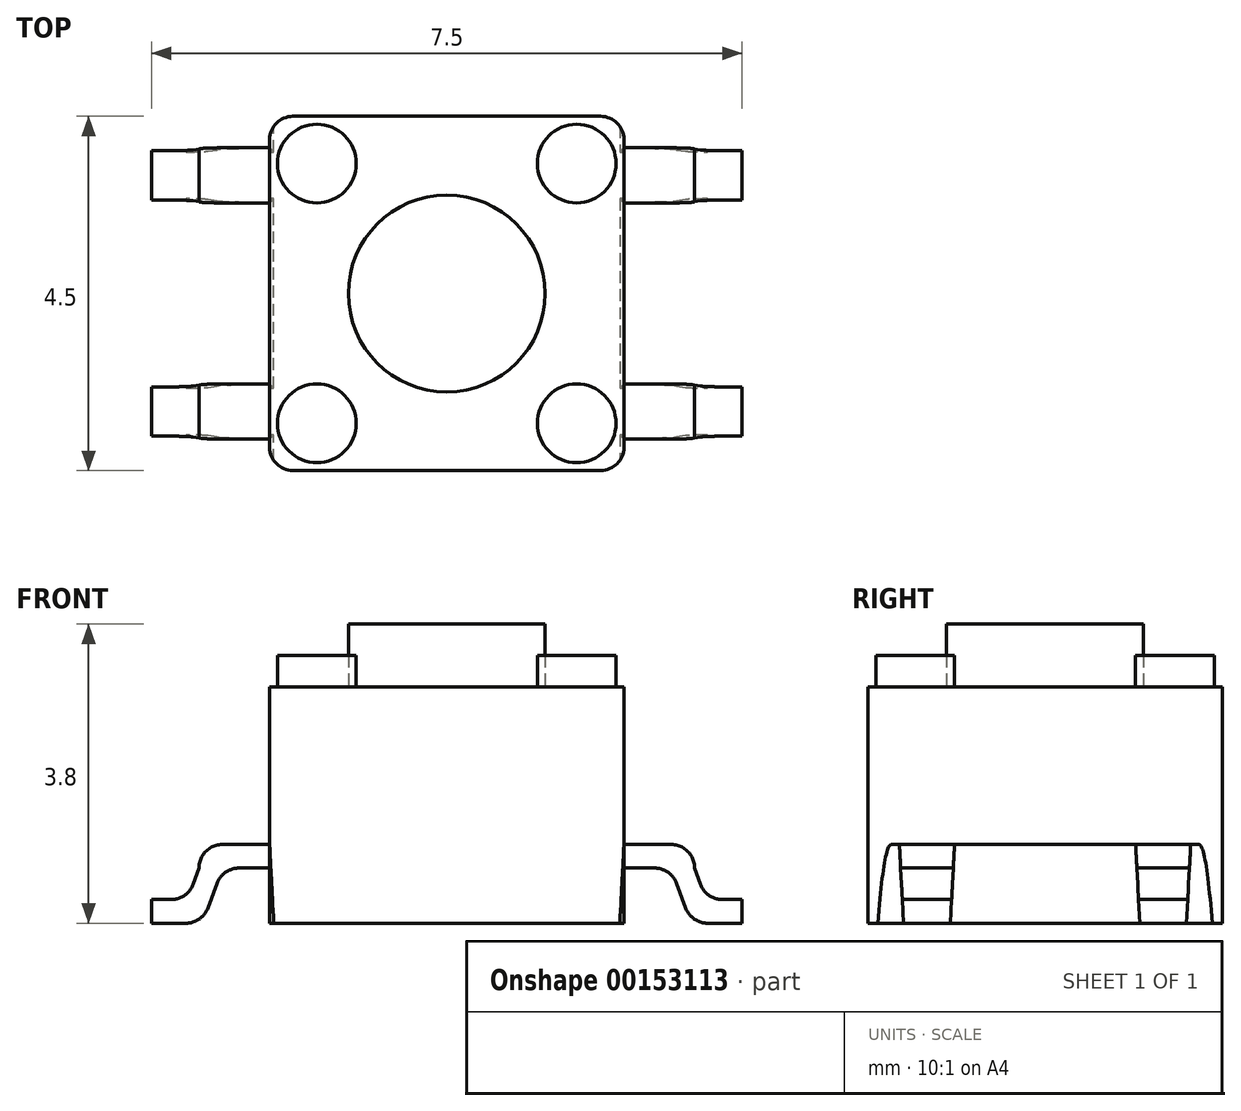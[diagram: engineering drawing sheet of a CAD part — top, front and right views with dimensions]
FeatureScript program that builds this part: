
annotation { "Feature Type Name" : "Feature", "Feature Type Description" : "" }
export const myFeature = defineFeature(function(context is Context, id is Id, definition is map)
    precondition{}
    {
        {
            var Q0;
            Q0=qCreatedBy(makeId("Top.planeOp"),FACE);
            var sketch = newSketch(context, id + "F0", { "sketchPlane" : qUnion([Q0])});
            skLineSegment(sketch, "E0.bottom", {"start": v(-1.96, 2.25) * mm, "end": v(1.96, 2.25) * mm});
            skLineSegment(sketch, "E0.top", {"start": v(-1.96, -2.25) * mm, "end": v(1.96, -2.25) * mm});
            skLineSegment(sketch, "E0.left", {"start": v(-2.25, 1.96) * mm, "end": v(-2.25, -1.96) * mm});
            skLineSegment(sketch, "E0.right", {"start": v(2.25, 1.96) * mm, "end": v(2.25, -1.96) * mm});
            skPoint(sketch, "E1.visualSharp", {"position": v(-2.25, 2.25) * mm});
            skArc(sketch, "E1.filletArc", {"start": v(-1.96, 2.25) * mm, "mid": v(-2.16, 2.16) * mm, "end": v(-2.25, 1.96) * mm});
            skPoint(sketch, "E2.visualSharp", {"position": v(-2.25, -2.25) * mm});
            skArc(sketch, "E2.filletArc", {"start": v(-2.25, -1.96) * mm, "mid": v(-2.16, -2.16) * mm, "end": v(-1.96, -2.25) * mm});
            skPoint(sketch, "E3.visualSharp", {"position": v(2.25, -2.25) * mm});
            skArc(sketch, "E3.filletArc", {"start": v(1.96, -2.25) * mm, "mid": v(2.16, -2.16) * mm, "end": v(2.25, -1.96) * mm});
            skPoint(sketch, "E4.visualSharp", {"position": v(2.25, 2.25) * mm});
            skArc(sketch, "E4.filletArc", {"start": v(2.25, 1.96) * mm, "mid": v(2.16, 2.16) * mm, "end": v(1.96, 2.25) * mm});
            skSolve(sketch);
        }
        {
            var Q0;
            Q0 = qSketchRegion(id + "F0", true);
            extrude(context, id + "F1", {"entities" : qUnion([Q0]), "depth" : 3 * mm});
        }
        {
            var Q0;
            Q0=makeQuery(id+"F1.opExtrude","CAP_FACE",FACE,{"disambiguationData":[OSD([sQuery(id+"F0.wireOp",EDGE,"E0.bottom"),sQuery(id+"F0.wireOp",EDGE,"E0.top"),sQuery(id+"F0.wireOp",EDGE,"E0.left"),sQuery(id+"F0.wireOp",EDGE,"E0.right"),sQuery(id+"F0.wireOp",EDGE,"E1.filletArc"),sQuery(id+"F0.wireOp",EDGE,"E2.filletArc"),sQuery(id+"F0.wireOp",EDGE,"E3.filletArc"),sQuery(id+"F0.wireOp",EDGE,"E4.filletArc")])],"isStart":false});
            var sketch = newSketch(context, id + "F2", { "sketchPlane" : qUnion([Q0])});
            skCircle(sketch, "E5", {"center": v(0, 0) * mm, "radius": 1.25 * mm});
            skSolve(sketch);
        }
        {
            var Q0;
            Q0 = qSketchRegion(id + "F2", true);
            extrude(context, id + "F3", {"entities" : qUnion([Q0]), "depth" : .8 * mm});
        }
        {
            var Q0;
            Q0=makeQuery(id+"F1.opExtrude","CAP_FACE",FACE,{"disambiguationData":[OSD([sQuery(id+"F0.wireOp",EDGE,"E0.bottom"),sQuery(id+"F0.wireOp",EDGE,"E0.top"),sQuery(id+"F0.wireOp",EDGE,"E0.left"),sQuery(id+"F0.wireOp",EDGE,"E0.right"),sQuery(id+"F0.wireOp",EDGE,"E1.filletArc"),sQuery(id+"F0.wireOp",EDGE,"E2.filletArc"),sQuery(id+"F0.wireOp",EDGE,"E3.filletArc"),sQuery(id+"F0.wireOp",EDGE,"E4.filletArc")])],"isStart":false});
            var sketch = newSketch(context, id + "F4", { "sketchPlane" : qUnion([Q0])});
            skCircle(sketch, "E6", {"center": v(-1.65, 1.65) * mm, "radius": 0.5 * mm});
            skCircle(sketch, "E7.MirrorC", {"center": v(1.65, 1.65) * mm, "radius": 0.5 * mm});
            skCircle(sketch, "E8.MirrorC", {"center": v(1.65, -1.65) * mm, "radius": 0.5 * mm});
            skCircle(sketch, "E9.MirrorC", {"center": v(-1.65, -1.65) * mm, "radius": 0.5 * mm});
            skSolve(sketch);
        }
        {
            var Q0;
            Q0 = qSketchRegion(id + "F4", true);
            extrude(context, id + "F5", {"entities" : qUnion([Q0]), "operationType" : NewBodyOperationType.ADD, "depth" : .4 * mm});
        }
        {
            var Q0;
            Q0=makeQuery(id+"F1.opExtrude","SWEPT_FACE",FACE,{"disambiguationData":[OSD([sQuery(id+"F0.wireOp",EDGE,"E0.top")])]});
            var sketch = newSketch(context, id + "F6", { "sketchPlane" : qUnion([Q0])});
            skLineSegment(sketch, "E10", {"start": v(-2.25, 3) * mm, "end": v(-2.25, 0) * mm});
            skLineSegment(sketch, "E11.left", {"start": v(-3.75, 0) * mm, "end": v(-3.75, 0.3) * mm});
            skLineSegment(sketch, "E12.right", {"start": v(-2.25, 1) * mm, "end": v(-2.25, 0.7) * mm});
            skLineSegment(sketch, "E13", {"start": v(-3.22, 0.5) * mm, "end": v(-3.15, 0.7) * mm});
            skLineSegment(sketch, "E14", {"start": v(-3, 0.3) * mm, "end": v(-2.92, 0.5) * mm});
            skLineSegment(sketch, "E15", {"start": v(-2.25, 1) * mm, "end": v(-2.85, 1) * mm});
            skLineSegment(sketch, "E16", {"start": v(-3.15, 0.7) * mm, "end": v(-3.15, 0.7) * mm});
            skLineSegment(sketch, "E17", {"start": v(-3, 0.3) * mm, "end": v(-3.04, 0.2) * mm});
            skLineSegment(sketch, "E18", {"start": v(-2.25, 0.7) * mm, "end": v(-2.64, 0.7) * mm});
            skLineSegment(sketch, "E19", {"start": v(-3.31, 0) * mm, "end": v(-3.75, 0) * mm});
            skLineSegment(sketch, "E20", {"start": v(-3.75, 0.3) * mm, "end": v(-3.5, 0.3) * mm});
            skPoint(sketch, "E21.visualSharp", {"position": v(-3.15, 1) * mm});
            skArc(sketch, "E21.filletArc", {"start": v(-2.85, 1) * mm, "mid": v(-3.06, 0.91) * mm, "end": v(-3.15, 0.7) * mm});
            skPoint(sketch, "E22.visualSharp", {"position": v(-3.1, 0) * mm});
            skArc(sketch, "E22.filletArc", {"start": v(-3.31, 0) * mm, "mid": v(-3.14, 0.05) * mm, "end": v(-3.04, 0.2) * mm});
            skPoint(sketch, "E23.visualSharp", {"position": v(-3.3, 0.3) * mm});
            skArc(sketch, "E23.filletArc", {"start": v(-3.5, 0.3) * mm, "mid": v(-3.33, 0.35) * mm, "end": v(-3.22, 0.5) * mm});
            skArc(sketch, "E24.filletArc", {"start": v(-2.64, 0.7) * mm, "mid": v(-2.8, 0.65) * mm, "end": v(-2.92, 0.5) * mm});
            skLineSegment(sketch, "E25.MirrorCS", {"start": v(3.15, 0.7) * mm, "end": v(3.15, 0.7) * mm});
            skLineSegment(sketch, "E26.MirrorCS", {"start": v(3, 0.3) * mm, "end": v(3.04, 0.2) * mm});
            skPoint(sketch, "E27.MirrorP", {"position": v(3.1, 0) * mm});
            skLineSegment(sketch, "E28.MirrorCS", {"start": v(2.25, 0.7) * mm, "end": v(2.64, 0.7) * mm});
            skArc(sketch, "E29.MirrorCS", {"start": v(2.85, 1) * mm, "mid": v(3.06, 0.91) * mm, "end": v(3.15, 0.7) * mm});
            skLineSegment(sketch, "E30.MirrorCS", {"start": v(2.25, 1) * mm, "end": v(2.85, 1) * mm});
            skPoint(sketch, "E31.MirrorP", {"position": v(3.15, 1) * mm});
            skPoint(sketch, "E32.MirrorP", {"position": v(3.3, 0.3) * mm});
            skLineSegment(sketch, "E33.MirrorCS", {"start": v(3.75, 0) * mm, "end": v(3.75, 0.3) * mm});
            skLineSegment(sketch, "E34.MirrorCS", {"start": v(3.75, 0.3) * mm, "end": v(3.5, 0.3) * mm});
            skArc(sketch, "E35.MirrorCS", {"start": v(3.5, 0.3) * mm, "mid": v(3.33, 0.35) * mm, "end": v(3.22, 0.5) * mm});
            skLineSegment(sketch, "E36.MirrorCS", {"start": v(3.31, 0) * mm, "end": v(3.75, 0) * mm});
            skLineSegment(sketch, "E37.MirrorCS", {"start": v(2.25, 1) * mm, "end": v(2.25, 0.7) * mm});
            skLineSegment(sketch, "E38.MirrorCS", {"start": v(3, 0.3) * mm, "end": v(2.92, 0.5) * mm});
            skLineSegment(sketch, "E39.MirrorCS", {"start": v(3.22, 0.5) * mm, "end": v(3.15, 0.7) * mm});
            skArc(sketch, "E40.MirrorCS", {"start": v(3.31, 0) * mm, "mid": v(3.14, 0.05) * mm, "end": v(3.04, 0.2) * mm});
            skArc(sketch, "E41.MirrorCS", {"start": v(2.64, 0.7) * mm, "mid": v(2.8, 0.65) * mm, "end": v(2.92, 0.5) * mm});
            skSolve(sketch);
        }
        {
            var Q0;
            Q0 = qSketchRegion(id + "F6", true);
            extrude(context, id + "F7", {"entities" : qUnion([Q0]), "oppositeDirection" : true, "depth" : 4.5 * mm});
        }
        {
            var Q0;
            Q0=makeQuery(id+"F7.opExtrude","SWEPT_FACE",FACE,{"disambiguationData":[OSD([sQuery(id+"F6.wireOp",EDGE,"E15")])]});
            var sketch = newSketch(context, id + "F8", { "sketchPlane" : qUnion([Q0])});
            skLineSegment(sketch, "E42.bottom", {"start": v(-2.25, 1.15) * mm, "end": v(-4.89, 1.15) * mm});
            skLineSegment(sketch, "E42.top", {"start": v(-2.25, -1.15) * mm, "end": v(-4.89, -1.15) * mm});
            skLineSegment(sketch, "E42.left", {"start": v(-2.25, 1.15) * mm, "end": v(-2.25, -1.15) * mm});
            skLineSegment(sketch, "E42.right", {"start": v(-4.89, 1.15) * mm, "end": v(-4.89, -1.15) * mm});
            skLineSegment(sketch, "E43.bottom", {"start": v(-4.89, -1.85) * mm, "end": v(-2.25, -1.85) * mm});
            skLineSegment(sketch, "E43.top", {"start": v(-4.89, -3.23) * mm, "end": v(-2.25, -3.23) * mm});
            skLineSegment(sketch, "E43.left", {"start": v(-4.89, -1.85) * mm, "end": v(-4.89, -3.23) * mm});
            skLineSegment(sketch, "E43.right", {"start": v(-2.25, -1.85) * mm, "end": v(-2.25, -3.23) * mm});
            skLineSegment(sketch, "E44.bottom", {"start": v(-4.89, 1.85) * mm, "end": v(-2.25, 1.85) * mm});
            skLineSegment(sketch, "E44.top", {"start": v(-4.89, 2.7) * mm, "end": v(-2.25, 2.7) * mm});
            skLineSegment(sketch, "E44.left", {"start": v(-4.89, 1.85) * mm, "end": v(-4.89, 2.7) * mm});
            skLineSegment(sketch, "E44.right", {"start": v(-2.25, 1.85) * mm, "end": v(-2.25, 2.7) * mm});
            skLineSegment(sketch, "E45.MirrorCS", {"start": v(2.25, 1.15) * mm, "end": v(4.89, 1.15) * mm});
            skLineSegment(sketch, "E46.MirrorCS", {"start": v(2.25, -1.15) * mm, "end": v(4.89, -1.15) * mm});
            skLineSegment(sketch, "E47.MirrorCS", {"start": v(2.25, 1.15) * mm, "end": v(2.25, -1.15) * mm});
            skLineSegment(sketch, "E48.MirrorCS", {"start": v(4.89, 1.15) * mm, "end": v(4.89, -1.15) * mm});
            skLineSegment(sketch, "E49.MirrorCS", {"start": v(4.89, -1.85) * mm, "end": v(2.25, -1.85) * mm});
            skLineSegment(sketch, "E50.MirrorCS", {"start": v(2.25, 1.85) * mm, "end": v(2.25, 2.7) * mm});
            skLineSegment(sketch, "E51.MirrorCS", {"start": v(4.89, -1.85) * mm, "end": v(4.89, -3.23) * mm});
            skLineSegment(sketch, "E52.MirrorCS", {"start": v(2.25, -1.85) * mm, "end": v(2.25, -3.23) * mm});
            skLineSegment(sketch, "E53.MirrorCS", {"start": v(4.89, 1.85) * mm, "end": v(2.25, 1.85) * mm});
            skLineSegment(sketch, "E54.MirrorCS", {"start": v(4.89, 2.7) * mm, "end": v(2.25, 2.7) * mm});
            skLineSegment(sketch, "E55.MirrorCS", {"start": v(4.89, -3.23) * mm, "end": v(2.25, -3.23) * mm});
            skLineSegment(sketch, "E56.MirrorCS", {"start": v(4.89, 1.85) * mm, "end": v(4.89, 2.7) * mm});
            skSolve(sketch);
        }
        {
            var Q0;
            Q0 = qSketchRegion(id + "F8", true);
            extrude(context, id + "F9", {"entities" : qUnion([Q0]), "operationType" : NewBodyOperationType.REMOVE, "endBound" : BoundingType.THROUGH_ALL, "oppositeDirection" : true, "depth" : 25 * mm, "hasDraft" : true, "draftAngle" : 3 * degree});
        }
    });
